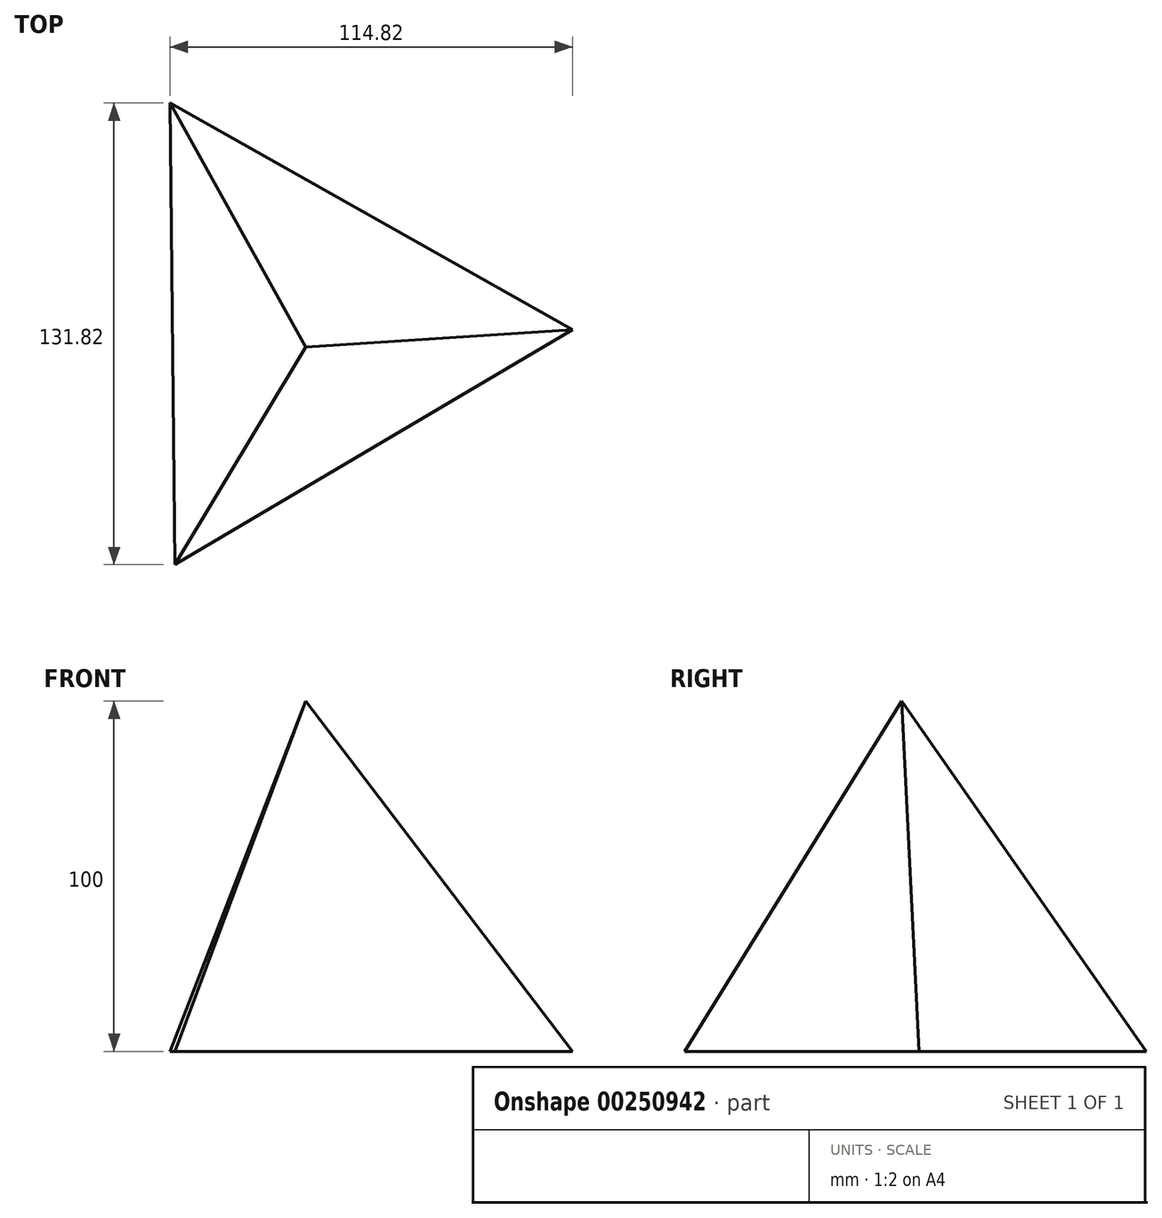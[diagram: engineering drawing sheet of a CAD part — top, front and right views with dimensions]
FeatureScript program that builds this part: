
annotation { "Feature Type Name" : "Feature", "Feature Type Description" : "" }
export const myFeature = defineFeature(function(context is Context, id is Id, definition is map)
    precondition{}
    {
        {
            var Q0;
            Q0=qCreatedBy(makeId("Top.planeOp"),FACE);
            var sketch = newSketch(context, id + "F0", { "sketchPlane" : qUnion([Q0])});
            skCircle(sketch, "E0.cCircle", {"center": v(0, 0) * mm, "radius": 76.11 * mm, "construction": true});
            skLineSegment(sketch, "E0.0", {"start": v(-38.7, 65.53) * mm, "end": v(76.1, 0.76) * mm});
            skLineSegment(sketch, "E0.1", {"start": v(76.1, 0.76) * mm, "end": v(-37.4, -66.29) * mm});
            skLineSegment(sketch, "E0.2", {"start": v(-37.4, -66.29) * mm, "end": v(-38.7, 65.53) * mm});
            skSolve(sketch);
        }
        {
            var Q0;
            Q0=qCreatedBy(makeId("Top.planeOp"),FACE);
            cPlane(context, id + "F1", {"entities" : qUnion([Q0]), "cplaneType" : CPlaneType.OFFSET, "offset" : 100 * mm, "width" : 150 * mm, "height" : 150 * mm});
        }
        {
            var Q0;
            Q0=qCreatedBy(id+"F1.planeOp",FACE);
            var sketch = newSketch(context, id + "F2", { "sketchPlane" : qUnion([Q0])});
            skPoint(sketch, "E1", {"position": v(0, -4.22) * mm});
            skSolve(sketch);
        }
        {
            var Q0;
            Q0=makeQuery(id+"F0.imprint","IMPRINT",FACE,{"disambiguationData":[TD([[makeQuery(id+"F0.imprint","IMPRINT",EDGE,{"derivedFrom":sQuery(id+"F0.wireOp",EDGE,"E0.0")}),-1.0]])]});
            var Q1;
            Q1=sQuery(id+"F2.wireOp",VERTEX,"E1");
            loft(context, id + "F3", {"sheetProfilesArray" : [{ "sheetProfileEntities" : qUnion([Q0]) }, { "sheetProfileEntities" : qUnion([Q1]) }]});
        }
    });
